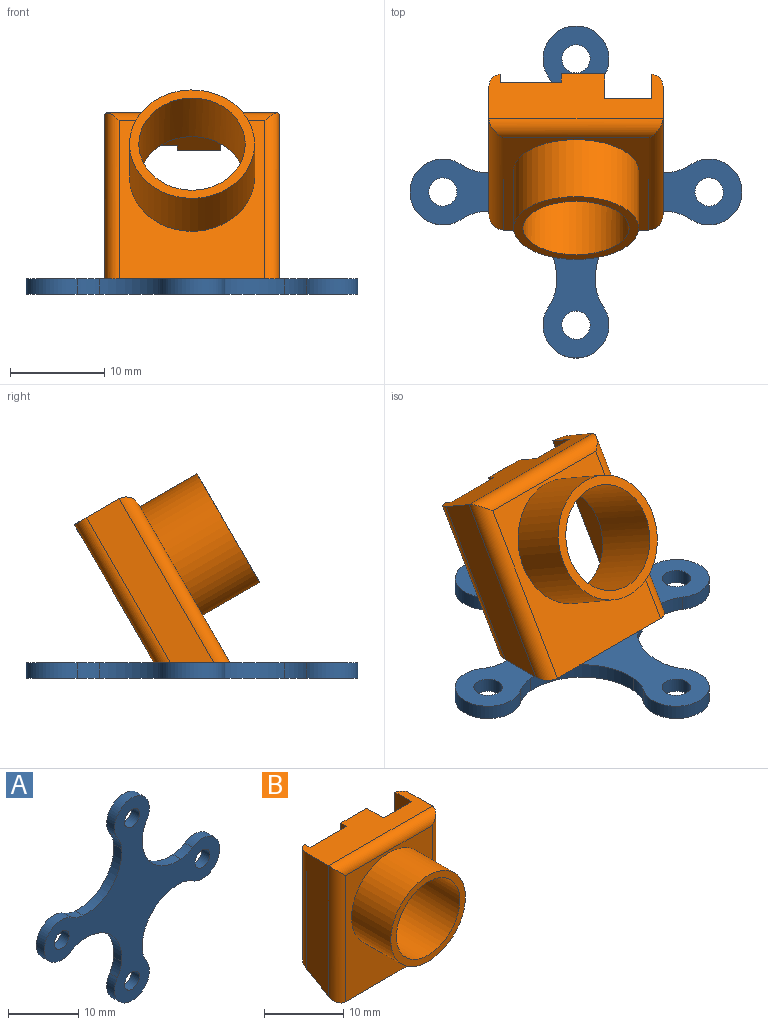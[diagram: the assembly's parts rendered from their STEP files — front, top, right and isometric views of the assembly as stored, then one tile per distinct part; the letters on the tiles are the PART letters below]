
ASSEMBLY  parts=2 mates=1
PART A: 22 faces, bbox 35.3x1.6x35.3 mm
  f0: cylinder r=5mm len=2.39mm, axis (0,1,0), area 4.1mm2, adj f1,f19,f20,f21
  f1: cylinder r=3.5mm len=7mm, axis (0,1,0), area 24.2mm2, adj f0,f2,f20,f21
  f2: cylinder r=5mm len=2.39mm, axis (0,1,0), area 4.1mm2, adj f1,f3,f20,f21
  f3: cylinder r=7.18mm len=7.75mm, axis (0,1,0), area 19.9mm2, adj f2,f4,f20,f21
  f4: cylinder r=5mm len=2.39mm, axis (0,1,0), area 4.1mm2, adj f3,f5,f20,f21
  f5: cylinder r=3.5mm len=7mm, axis (0,1,0), area 24.2mm2, adj f4,f6,f20,f21
  f6: cylinder r=5mm len=2.39mm, axis (0,1,0), area 4.1mm2, adj f5,f7,f20,f21
  f7: cylinder r=7.18mm len=7.75mm, axis (0,1,0), area 19.9mm2, adj f6,f8,f20,f21
  f8: cylinder r=5mm len=2.39mm, axis (0,1,0), area 4.1mm2, adj f7,f9,f20,f21
  f9: cylinder r=3.5mm len=7mm, axis (0,1,0), area 24.2mm2, adj f8,f10,f20,f21
  f10: cylinder r=5mm len=2.39mm, axis (0,1,0), area 4.1mm2, adj f9,f11,f20,f21
  f11: cylinder r=7.18mm len=7.75mm, axis (0,1,0), area 19.9mm2, adj f10,f12,f20,f21
  f12: cylinder r=5mm len=2.39mm, axis (0,1,0), area 4.1mm2, adj f11,f13,f20,f21
  f13: cylinder r=3.5mm len=7mm, axis (0,1,0), area 24.2mm2, adj f12,f14,f20,f21
  f14: cylinder r=5mm len=2.39mm, axis (0,1,0), area 4.1mm2, adj f13,f19,f20,f21
  f15: cylinder r=1.5mm len=3mm, axis (0,1,0), area 15.1mm2, adj f20,f21
  f16: cylinder r=1.5mm len=3mm, axis (0,1,0), area 15.1mm2, adj f20,f21
  f17: cylinder r=1.5mm len=3mm, axis (0,1,0), area 15.1mm2, adj f20,f21
  f18: cylinder r=1.5mm len=3mm, axis (0,1,0), area 15.1mm2, adj f20,f21
  f19: cylinder r=7.18mm len=7.75mm, axis (0,1,0), area 19.9mm2, adj f0,f14,f20,f21
  f20: plane 35.28x35.28mm, normal (0,-1,0), area 333.8mm2, adj f0,f1,f2,f3,f4,f5,f6,f7
  f21: plane 35.28x35.28mm, normal (0,1,0), area 333.8mm2, adj f0,f1,f2,f3,f4,f5,f6,f7
PART B: 24 faces, bbox 18.5x14x21 mm
  f0: plane 15.5x1.16mm, normal (0,1,0), area 18mm2, adj f7,f18,f19,f20
  f1: plane 20.13x4mm, normal (-1,0,0), area 75.9mm2, adj f2,f18,f20,f22
  f2: plane 18.5x5.5mm, normal (0,0,1), area 79.3mm2, adj f1,f4,f5,f8,f9,f14,f15,f16
  f3: plane 16.1x5.8mm, normal (0,0,-1), area 71.9mm2, adj f4,f8,f9,f10,f14,f15,f16,f17
  f4: plane 4.6x1.2mm, normal (0,1,0), area 5.5mm2, adj f2,f3,f14,f16
  f5: plane 20.13x4mm, normal (1,0,0), area 75.9mm2, adj f2,f18,f19,f21
  f6: plane 19.5x15.5mm, normal (0,-1,0), area 163.3mm2, adj f12,f18,f21,f22,f23
  f7: plane 16.1x5.8mm, normal (0,0,1), area 93.4mm2, adj f0,f8,f9,f10,f19,f20
  f8: plane 15.8x5.77mm, normal (-1,0,0), area 87.8mm2, adj f2,f3,f7,f10,f15,f19
  f9: plane 15.8x5.77mm, normal (1,0,0), area 85.4mm2, adj f2,f3,f7,f10,f17,f20
  f10: plane 16.1x14.6mm, normal (0,1,0), area 134.8mm2, adj f3,f7,f8,f9,f11
  f11: cylinder r=5.65mm len=11.3mm, axis (0,-1,0), area 291.1mm2, adj f10,f13
  f12: cylinder r=6.65mm len=13.3mm, axis (0,1,0), area 292.5mm2, adj f6,f13
  f13: plane 13.3x13.3mm, normal (0,-1,0), area 38.6mm2, adj f11,f12
  f14: plane 3x1.2mm, normal (1,0,0), area 3.6mm2, adj f2,f3,f4,f15
  f15: plane 5x1.2mm, normal (0,1,0), area 6mm2, adj f2,f3,f8,f14
  f16: plane 1.2x1mm, normal (-1,0,0), area 1.2mm2, adj f2,f3,f4,f17
  f17: plane 6.5x1.2mm, normal (0,1,0), area 7.8mm2, adj f2,f3,f9,f16
  f18: plane 18.5x7mm, normal (0,0.5,-0.87), area 147.3mm2, adj f0,f1,f5,f6,f19,f20,f21,f22
  f19: cylinder r=1.5mm len=17.82mm, axis (0,0,1), area 35.9mm2, adj f0,f2,f5,f7,f8,f18
  f20: cylinder r=1.5mm len=17.82mm, axis (0,0,-1), area 35.9mm2, adj f0,f1,f2,f7,f9,f18
  f21: cylinder r=1.5mm len=21mm, axis (0,0,-1), area 47.5mm2, adj f5,f6,f18,f23
  f22: cylinder r=1.5mm len=21mm, axis (0,0,1), area 47.5mm2, adj f1,f6,f18,f23
  f23: cylinder r=1.5mm len=18.5mm, axis (1,0,0), area 41mm2, adj f2,f6,f21,f22
PLACE A rot(axis=(1,0,0),90deg) t=(0,-1.15,2.07)mm
PLACE B rot(axis=(-1,0,0),30deg) t=(0,7.12,9.39)mm
MATE fastened B.f18 <-> A.f21  axis (0,0,-1) through (0,-1.15,2.07)mm
